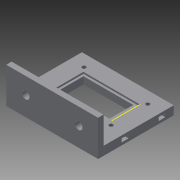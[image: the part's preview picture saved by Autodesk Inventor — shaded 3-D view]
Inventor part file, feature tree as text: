
AUTODESK INVENTOR PART (.ipt)
format: ipt  version: 2015 (Build 190159000, 159)  size: 203,776 bytes
history: native  units: in
note: dims shown in document units (in); Inventor stores cm internally (conversion verified against a paired STEP export)
features: extrude x9, sketch x9
ambient origin geometry x8: Origin, YZ Plane, XZ Plane, XY Plane, X Axis, Y Axis, Z Axis, Center Point
bodies: Solid1 (feature_tree)
feature tree (18):
  extrude  "Extrusion1"  Depth=3.3465in
  extrude  "Extrusion2"  TaperAngle=0.0deg  [1 undecoded]
  extrude  "Extrusion3"  Depth=0.1969in
  extrude  "Extrusion4"  Depth=0.0591in TaperAngle=0.0deg
  extrude  "Extrusion9"  Depth=0.0787in
  sketch  "Sketch16"  dims[d20=0.0787in d21=0.0787in]
  extrude  "Extrusion14"  Depth=0.1575in
  extrude  "Extrusion16"  Depth=0.6004in
  extrude  "Extrusion17"  Depth=0.2756in
  extrude  "Extrusion18"  Depth=0.1969in TaperAngle=0.0deg
  sketch  "Sketch1"  dims[d4=2.7559in d5=3.3465in]
  sketch  "Sketch2"  dims[d6=1.2992in d7=0.0in d8=0.0in]
  sketch  "Sketch4"  dims[d9=0.0in d10=0.1969in]
  sketch  "Sketch10"  dims[d12=0.9843in d13=0.0in d18=0.0591in d19=0.0in]
  sketch  "Sketch17"  dims[d22=0.0787in d23=0.1575in]
  sketch  "Sketch20"  dims[d24=0.0394in d25=0.0in d53=0.6004in]
  sketch  "Sketch21"  dims[d55=0.6004in d58=0.2756in]
  sketch  "Sketch22"  dims[d59=0.2756in d60=0.1969in d61=0.0in d70=1.9291in d71=0.7087in d93=0.0in d94=0.0in d95=0.0in d96=0.0in d97=0.1969in d98=0.0in d106=1.0236in d107=0.1378in d110=1.3386in d111=2.3228in d113=0.128in d125=0.2461in d130=0.6299in d131=0.0in d136=0.6299in d137=0.0in d141=0.0in d142=0.0in d144=2.0472in d145=0.5906in]
note: 1 required parameter value undecoded (feature->parameter linkage not recoverable at this tier; creation-order binding heuristic only, values carry confidence <= 0.55)
